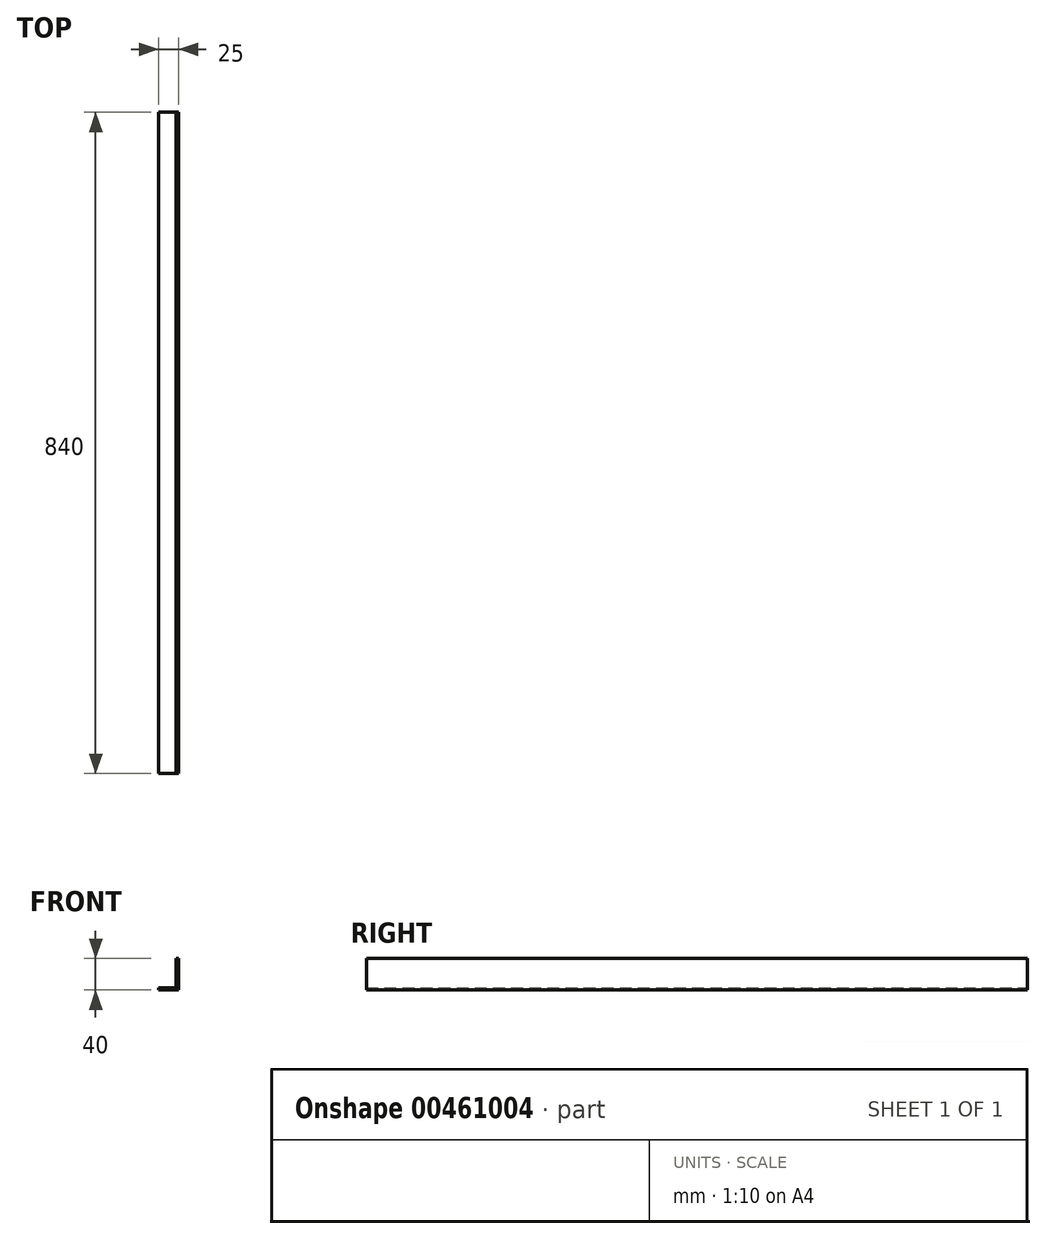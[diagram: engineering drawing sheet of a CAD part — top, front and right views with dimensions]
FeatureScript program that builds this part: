
annotation { "Feature Type Name" : "Feature", "Feature Type Description" : "" }
export const myFeature = defineFeature(function(context is Context, id is Id, definition is map)
    precondition{}
    {
        {
            var Q0;
            Q0=qCreatedBy(makeId("Front.planeOp"),FACE);
            var sketch = newSketch(context, id + "F0", { "sketchPlane" : qUnion([Q0])});
            skLineSegment(sketch, "E0", {"start": v(0, 0) * mm, "end": v(25, 0) * mm});
            skLineSegment(sketch, "E1", {"start": v(25, 0) * mm, "end": v(25, 40) * mm});
            skLineSegment(sketch, "E2", {"start": v(25, 40) * mm, "end": v(22, 40) * mm});
            skLineSegment(sketch, "E3", {"start": v(22, 40) * mm, "end": v(22, 3) * mm});
            skLineSegment(sketch, "E4", {"start": v(22, 3) * mm, "end": v(0, 3) * mm});
            skLineSegment(sketch, "E5", {"start": v(0, 3) * mm, "end": v(0, 0) * mm});
            skSolve(sketch);
        }
        {
            var Q0;
            Q0 = qSketchRegion(id + "F0", true);
            extrude(context, id + "F1", {"entities" : qUnion([Q0]), "depth" : 840 * mm});
        }
    });
